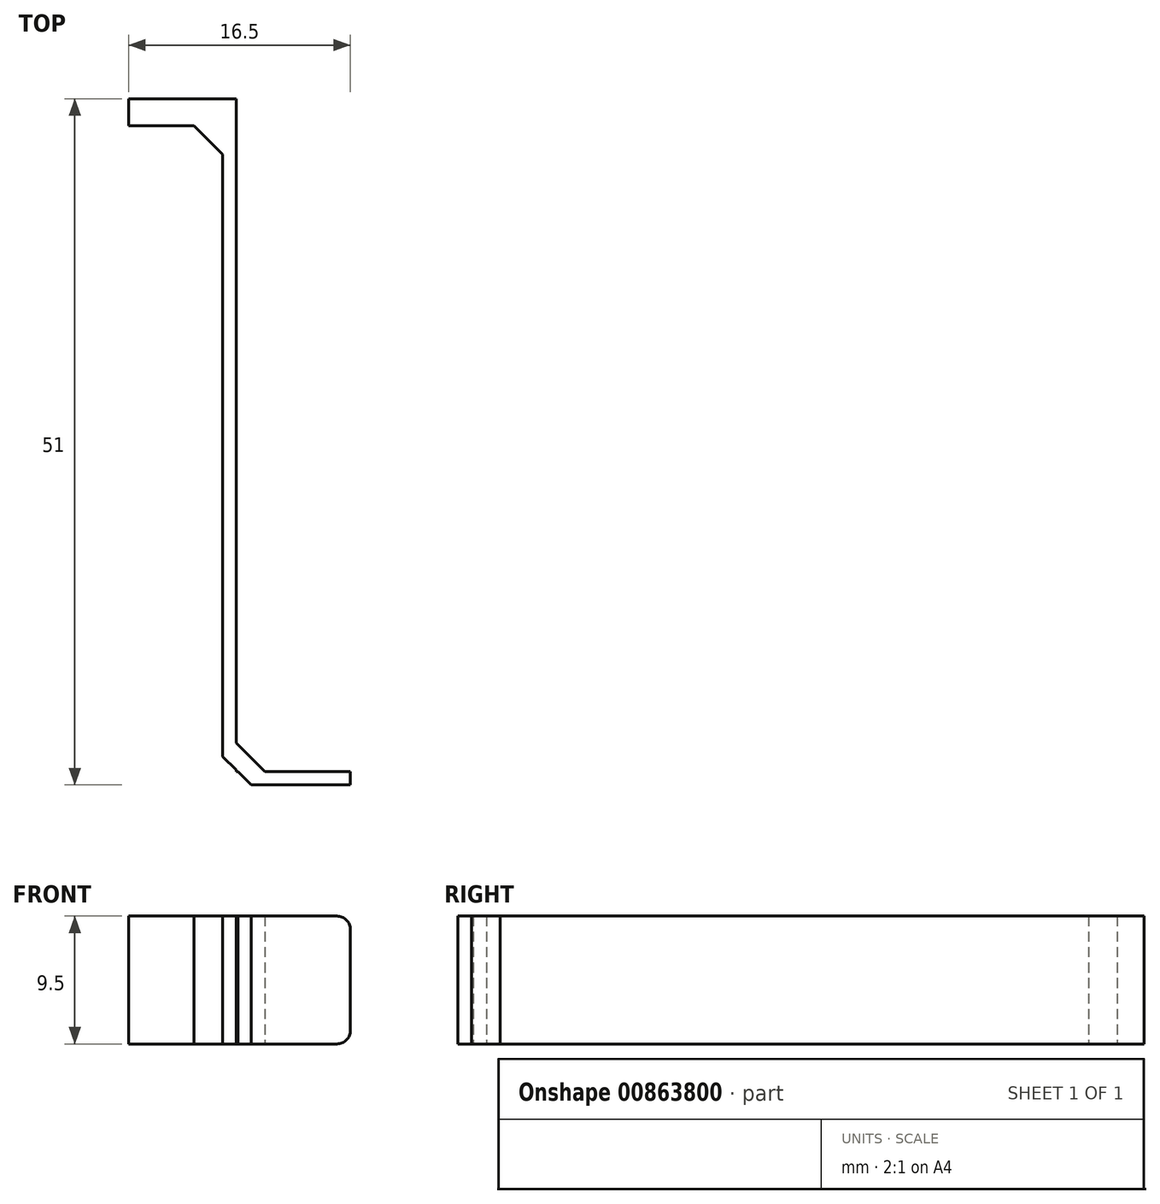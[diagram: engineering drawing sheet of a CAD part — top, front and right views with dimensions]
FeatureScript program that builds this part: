
annotation { "Feature Type Name" : "Feature", "Feature Type Description" : "" }
export const myFeature = defineFeature(function(context is Context, id is Id, definition is map)
    precondition{}
    {
        {
            var Q0;
            Q0=qCreatedBy(makeId("Top.planeOp"),FACE);
            var sketch = newSketch(context, id + "F0", { "sketchPlane" : qUnion([Q0])});
            skLineSegment(sketch, "E0", {"start": v(0, 49) * mm, "end": v(0, 2.12) * mm});
            skLineSegment(sketch, "E1", {"start": v(0, 0) * mm, "end": v(2.12, 0) * mm, "construction": true});
            skLineSegment(sketch, "E2", {"start": v(9.5, 0) * mm, "end": v(9.5, 1) * mm});
            skLineSegment(sketch, "E3", {"start": v(9.5, 1) * mm, "end": v(1, 1) * mm});
            skLineSegment(sketch, "E4", {"start": v(1, 1) * mm, "end": v(1, 51) * mm});
            skLineSegment(sketch, "E5", {"start": v(3.12, 1) * mm, "end": v(1, 3.12) * mm});
            skLineSegment(sketch, "E6", {"start": v(-7, 49) * mm, "end": v(0, 49) * mm});
            skLineSegment(sketch, "E7", {"start": v(-7, 49) * mm, "end": v(-7, 51) * mm});
            skLineSegment(sketch, "E8", {"start": v(1, 51) * mm, "end": v(-7, 51) * mm});
            skLineSegment(sketch, "E9", {"start": v(-2.12, 49) * mm, "end": v(0, 46.88) * mm});
            skLineSegment(sketch, "E10", {"start": v(0, 2.12) * mm, "end": v(0, 0) * mm, "construction": true});
            skLineSegment(sketch, "E11", {"start": v(2.12, 0) * mm, "end": v(9.5, 0) * mm});
            skLineSegment(sketch, "E12", {"start": v(2.12, 0) * mm, "end": v(0, 2.12) * mm});
            skSolve(sketch);
        }
        {
            var Q0;
            Q0 = qSketchRegion(id + "F0", true);
            extrude(context, id + "F1", {"entities" : qUnion([Q0]), "depth" : 9.5 * mm, "offsetDistance" : 25 * mm});
        }
        {
            var Q0;
            Q0=makeQuery(id+"F1.opExtrude","CAP_EDGE",EDGE,{"disambiguationData":[OSD([sQuery(id+"F0.wireOp",EDGE,"E2")])],"isStart":false});
            var Q1;
            Q1=makeQuery(id+"F1.opExtrude","CAP_EDGE",EDGE,{"disambiguationData":[OSD([sQuery(id+"F0.wireOp",EDGE,"E2")])],"isStart":true});
            fillet(context, id + "F2", {"entities" : qUnion([Q0, Q1]), "tangentPropagation" : true, "radius" : 1 * mm, "defaultsChanged" : true, "vertexSettings" : [], "allowEdgeOverflow" : false});
        }
    });
